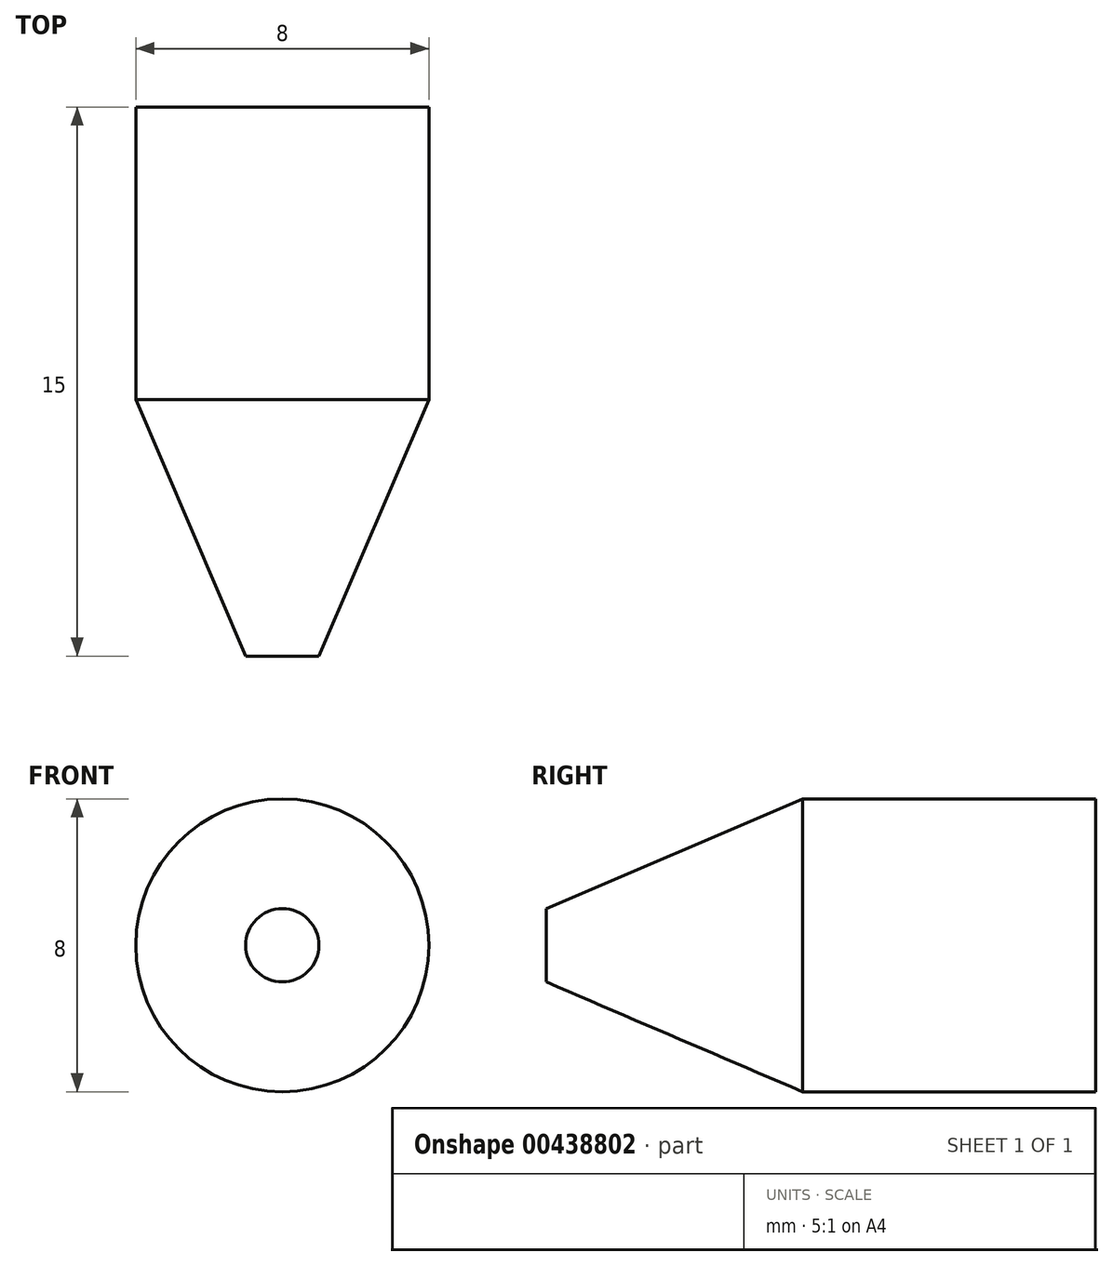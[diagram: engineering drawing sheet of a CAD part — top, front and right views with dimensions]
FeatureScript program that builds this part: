
annotation { "Feature Type Name" : "Feature", "Feature Type Description" : "" }
export const myFeature = defineFeature(function(context is Context, id is Id, definition is map)
    precondition{}
    {
        {
            var Q0;
            Q0=qCreatedBy(makeId("Front.planeOp"),FACE);
            var sketch = newSketch(context, id + "F0", { "sketchPlane" : qUnion([Q0])});
            skCircle(sketch, "E0", {"center": v(0, 0) * mm, "radius": 4 * mm});
            skSolve(sketch);
        }
        {
            var Q0;
            Q0 = qSketchRegion(id + "F0", true);
            extrude(context, id + "F1", {"entities" : qUnion([Q0]), "depth" : 15 * mm, "offsetDistance" : 25 * mm});
        }
        {
            var Q0;
            Q0=makeQuery(id+"F1.opExtrude","CAP_EDGE",EDGE,{"disambiguationData":[OSD([sQuery(id+"F0.wireOp",EDGE,"E0")])],"isStart":false});
            chamfer(context, id + "F2", {"entities" : qUnion([Q0]), "chamferType" : ChamferType.TWO_OFFSETS, "width1" : 3 * mm, "oppositeDirection" : false, "width2" : 7 * mm, "tangentPropagation" : true});
        }
    });
